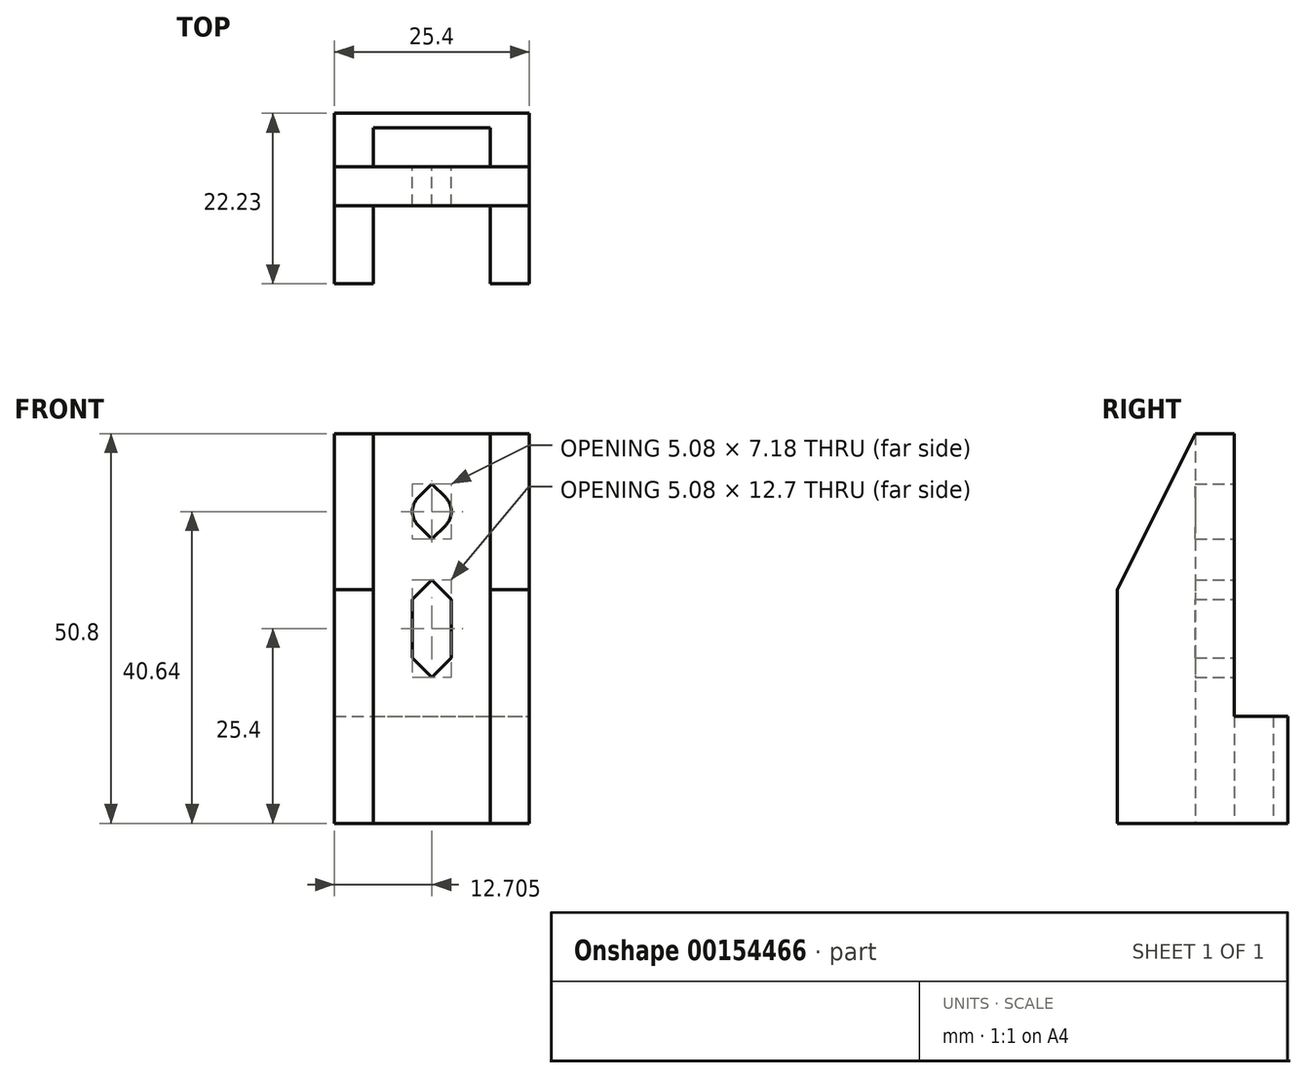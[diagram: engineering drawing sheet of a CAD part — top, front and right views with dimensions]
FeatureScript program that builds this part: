
annotation { "Feature Type Name" : "Feature", "Feature Type Description" : "" }
export const myFeature = defineFeature(function(context is Context, id is Id, definition is map)
    precondition{}
    {
        {
            var Q0;
            Q0=qCreatedBy(makeId("Top.planeOp"),FACE);
            var sketch = newSketch(context, id + "F0", { "sketchPlane" : qUnion([Q0])});
            skLineSegment(sketch, "E0.bottom", {"start": v(-5.07, -11.68) * mm, "end": v(10.17, -11.68) * mm});
            skLineSegment(sketch, "E0.top", {"start": v(-5.07, -6.6) * mm, "end": v(10.17, -6.6) * mm});
            skLineSegment(sketch, "E0.left", {"start": v(-5.07, -11.68) * mm, "end": v(-5.07, -6.6) * mm});
            skLineSegment(sketch, "E0.right", {"start": v(10.17, -11.68) * mm, "end": v(10.17, -6.6) * mm});
            skLineSegment(sketch, "E1.bottom", {"start": v(-10.15, -16.76) * mm, "end": v(15.25, -16.76) * mm});
            skLineSegment(sketch, "E1.top", {"start": v(-10.15, -4.7) * mm, "end": v(15.25, -4.7) * mm});
            skLineSegment(sketch, "E1.left", {"start": v(-10.15, -16.76) * mm, "end": v(-10.15, -4.7) * mm});
            skLineSegment(sketch, "E1.right", {"start": v(15.25, -16.76) * mm, "end": v(15.25, -4.7) * mm});
            skSolve(sketch);
        }
        {
            var Q0;
            Q0=makeQuery(id+"F0.imprint","IMPRINT",FACE,{"disambiguationData":[TD([[makeQuery(id+"F0.imprint","IMPRINT",EDGE,{"derivedFrom":sQuery(id+"F0.wireOp",EDGE,"E0.bottom")}),-1.0]])]});
            extrude(context, id + "F1", {"entities" : qUnion([Q0]), "depth" : 101.6 * mm});
        }
        {
            var Q0;
            Q0=qCreatedBy(makeId("Top.planeOp"),FACE);
            var sketch = newSketch(context, id + "F6", { "sketchPlane" : qUnion([Q0])});
            skLineSegment(sketch, "E2.bottom", {"start": v(-10.15, -16.76) * mm, "end": v(-5.07, -16.76) * mm});
            skLineSegment(sketch, "E2.top", {"start": v(-10.15, -26.92) * mm, "end": v(-5.07, -26.92) * mm});
            skLineSegment(sketch, "E2.left", {"start": v(-10.15, -16.76) * mm, "end": v(-10.15, -26.92) * mm});
            skLineSegment(sketch, "E2.right", {"start": v(-5.07, -16.76) * mm, "end": v(-5.07, -26.92) * mm});
            skLineSegment(sketch, "E3.bottom", {"start": v(15.25, -16.76) * mm, "end": v(10.17, -16.76) * mm});
            skLineSegment(sketch, "E3.top", {"start": v(15.25, -26.92) * mm, "end": v(10.17, -26.92) * mm});
            skLineSegment(sketch, "E3.left", {"start": v(15.25, -16.76) * mm, "end": v(15.25, -26.92) * mm});
            skLineSegment(sketch, "E3.right", {"start": v(10.17, -16.76) * mm, "end": v(10.17, -26.92) * mm});
            skSolve(sketch);
        }
        {
            var Q0;
            Q0=qSketchRegion(id+"F6",true);
            var Q1;
            Q1=makeQuery(id+"F1.opExtrude","CAP_FACE",FACE,{"disambiguationData":[OSD([sQuery(id+"F0.wireOp",EDGE,"E0.bottom"),sQuery(id+"F0.wireOp",EDGE,"E0.top"),sQuery(id+"F0.wireOp",EDGE,"E0.left"),sQuery(id+"F0.wireOp",EDGE,"E0.right"),sQuery(id+"F0.wireOp",EDGE,"E1.bottom"),sQuery(id+"F0.wireOp",EDGE,"E1.top"),sQuery(id+"F0.wireOp",EDGE,"E1.left"),sQuery(id+"F0.wireOp",EDGE,"E1.right")])],"isStart":false});
            extrude(context, id + "F2", {"entities" : qUnion([Q0]), "operationType" : NewBodyOperationType.ADD, "endBound" : BoundingType.UP_TO_SURFACE, "endBoundEntityFace" : qUnion([Q1]), "depth" : 25.4 * mm});
        }
        {
            var Q0;
            Q0=makeQuery(id+"F2.boolean.opBoolean","MERGE",FACE,{"derivedFrom":[makeQuery(id+"F1.opExtrude","SWEPT_FACE",FACE,{"disambiguationData":[OSD([sQuery(id+"F0.wireOp",EDGE,"E1.right")])]}),makeQuery(id+"F2.opExtrude","SWEPT_FACE",FACE,{"disambiguationData":[OSD([sQuery(id+"F6.wireOp",EDGE,"E3.left")])]})]});
            var sketch = newSketch(context, id + "F3", { "sketchPlane" : qUnion([Q0])});
            skLineSegment(sketch, "E4.bottom", {"start": v(-4.7, 101.6) * mm, "end": v(-11.68, 101.6) * mm});
            skLineSegment(sketch, "E4.top", {"start": v(-4.7, 13.97) * mm, "end": v(-11.68, 13.97) * mm});
            skLineSegment(sketch, "E4.left", {"start": v(-4.7, 101.6) * mm, "end": v(-4.7, 13.97) * mm});
            skLineSegment(sketch, "E4.right", {"start": v(-11.68, 101.6) * mm, "end": v(-11.68, 13.97) * mm});
            skSolve(sketch);
        }
        {
            var Q0;
            Q0=qSketchRegion(id+"F3",true);
            var Q1;
            Q1=makeQuery(id+"F2.boolean.opBoolean","MERGE",FACE,{"derivedFrom":[makeQuery(id+"F1.opExtrude","SWEPT_FACE",FACE,{"disambiguationData":[OSD([sQuery(id+"F0.wireOp",EDGE,"E1.left")])]}),makeQuery(id+"F2.opExtrude","SWEPT_FACE",FACE,{"disambiguationData":[OSD([sQuery(id+"F6.wireOp",EDGE,"E2.left")])]})]});
            extrude(context, id + "F7", {"entities" : qUnion([Q0]), "operationType" : NewBodyOperationType.REMOVE, "endBound" : BoundingType.UP_TO_SURFACE, "oppositeDirection" : true, "endBoundEntityFace" : qUnion([Q1]), "depth" : 25.4 * mm});
        }
        {
            var Q0;
            Q0=makeQuery(id+"F2.boolean.opBoolean","MERGE",FACE,{"derivedFrom":[makeQuery(id+"F1.opExtrude","SWEPT_FACE",FACE,{"disambiguationData":[OSD([sQuery(id+"F0.wireOp",EDGE,"E1.right")])]}),makeQuery(id+"F2.opExtrude","SWEPT_FACE",FACE,{"disambiguationData":[OSD([sQuery(id+"F6.wireOp",EDGE,"E3.left")])]})]});
            var sketch = newSketch(context, id + "F4", { "sketchPlane" : qUnion([Q0])});
            skLineSegment(sketch, "E5", {"start": v(-26.92, 101.6) * mm, "end": v(-11.68, 101.6) * mm});
            skLineSegment(sketch, "E6", {"start": v(-11.68, 101.6) * mm, "end": v(-11.68, 101.6) * mm});
            skLineSegment(sketch, "E7", {"start": v(-11.68, 50.8) * mm, "end": v(-11.68, 101.6) * mm});
            skLineSegment(sketch, "E8", {"start": v(-16.76, 50.8) * mm, "end": v(-26.92, 30.48) * mm});
            skLineSegment(sketch, "E9", {"start": v(-26.92, 30.48) * mm, "end": v(-26.92, 101.6) * mm});
            skLineSegment(sketch, "E10", {"start": v(-11.68, 50.8) * mm, "end": v(-16.76, 50.8) * mm});
            skSolve(sketch);
        }
        {
            var Q0;
            Q0=makeQuery(id+"F4.imprint","IMPRINT",FACE,{"disambiguationData":[TD([[makeQuery(id+"F4.imprint","IMPRINT",EDGE,{"derivedFrom":sQuery(id+"F4.wireOp",EDGE,"E5")}),-1.0]])]});
            var Q1;
            Q1=makeQuery(id+"F2.boolean.opBoolean","MERGE",FACE,{"derivedFrom":[makeQuery(id+"F1.opExtrude","SWEPT_FACE",FACE,{"disambiguationData":[OSD([sQuery(id+"F0.wireOp",EDGE,"E1.left")])]}),makeQuery(id+"F2.opExtrude","SWEPT_FACE",FACE,{"disambiguationData":[OSD([sQuery(id+"F6.wireOp",EDGE,"E2.left")])]})]});
            extrude(context, id + "F8", {"entities" : qUnion([Q0]), "operationType" : NewBodyOperationType.REMOVE, "endBound" : BoundingType.UP_TO_SURFACE, "oppositeDirection" : true, "endBoundEntityFace" : qUnion([Q1]), "depth" : 25.4 * mm});
        }
        {
            var Q0;
            Q0=makeQuery(id+"F7.boolean.opBoolean","MERGE",FACE,{"derivedFrom":[makeQuery(id+"F1.opExtrude","SWEPT_FACE",FACE,{"disambiguationData":[OSD([sQuery(id+"F0.wireOp",EDGE,"E0.bottom")])]}),makeQuery(id+"F7.opExtrude","SWEPT_FACE",FACE,{"disambiguationData":[OSD([sQuery(id+"F3.wireOp",EDGE,"E4.right")])]})]});
            var sketch = newSketch(context, id + "F9", { "sketchPlane" : qUnion([Q0])});
            skCircle(sketch, "E11", {"center": v(-2.55, 40.64) * mm, "radius": 2.54 * mm});
            skCircle(sketch, "E12", {"center": v(-2.55, 25.4) * mm, "radius": 2.54 * mm});
            skLineSegment(sketch, "E13", {"start": v(-2.55, 40.64) * mm, "end": v(-2.55, 25.4) * mm, "construction": true});
            skLineSegment(sketch, "E14", {"start": v(-15.25, 40.64) * mm, "end": v(-2.55, 40.64) * mm, "construction": true});
            skLineSegment(sketch, "E15", {"start": v(10.15, 40.64) * mm, "end": v(-2.55, 40.64) * mm, "construction": true});
            skSolve(sketch);
        }
        {
            var Q0;
            Q0=qSketchRegion(id+"F9",true);
            extrude(context, id + "F5", {"entities" : qUnion([Q0]), "operationType" : NewBodyOperationType.REMOVE, "endBound" : BoundingType.UP_TO_NEXT, "oppositeDirection" : true, "depth" : 25.4 * mm});
        }
        {
            var Q0;
            Q0=makeQuery(id+"F7.boolean.opBoolean","MERGE",FACE,{"derivedFrom":[makeQuery(id+"F1.opExtrude","SWEPT_FACE",FACE,{"disambiguationData":[OSD([sQuery(id+"F0.wireOp",EDGE,"E0.bottom")])]}),makeQuery(id+"F7.opExtrude","SWEPT_FACE",FACE,{"disambiguationData":[OSD([sQuery(id+"F3.wireOp",EDGE,"E4.right")])]})]});
            var sketch = newSketch(context, id + "F10", { "sketchPlane" : qUnion([Q0])});
            skLineSegment(sketch, "E16.bottom", {"start": v(-0.01, 29.21) * mm, "end": v(-5.1, 29.21) * mm, "construction": true});
            skLineSegment(sketch, "E16.top", {"start": v(-0.01, 21.6) * mm, "end": v(-5.1, 21.6) * mm, "construction": true});
            skLineSegment(sketch, "E16.left", {"start": v(-0.01, 29.21) * mm, "end": v(-0.01, 21.6) * mm});
            skLineSegment(sketch, "E16.right", {"start": v(-5.1, 29.21) * mm, "end": v(-5.1, 21.6) * mm});
            skPoint(sketch, "E16.middle", {"position": v(-2.55, 25.4) * mm});
            skLineSegment(sketch, "E17", {"start": v(-5.1, 29.21) * mm, "end": v(-2.55, 31.75) * mm});
            skLineSegment(sketch, "E18", {"start": v(-2.55, 31.75) * mm, "end": v(-2.55, 31.75) * mm});
            skLineSegment(sketch, "E19", {"start": v(-0.01, 29.21) * mm, "end": v(-2.55, 31.75) * mm});
            skLineSegment(sketch, "E20", {"start": v(-0.01, 21.6) * mm, "end": v(-2.55, 19.05) * mm});
            skLineSegment(sketch, "E21", {"start": v(-2.55, 19.05) * mm, "end": v(-2.55, 19.05) * mm});
            skLineSegment(sketch, "E22", {"start": v(-2.55, 19.05) * mm, "end": v(-5.1, 21.59) * mm});
            skLineSegment(sketch, "E23", {"start": v(-4.35, 42.44) * mm, "end": v(-2.55, 44.23) * mm});
            skLineSegment(sketch, "E24", {"start": v(-2.55, 44.23) * mm, "end": v(-0.76, 42.44) * mm});
            skLineSegment(sketch, "E25", {"start": v(-4.35, 38.84) * mm, "end": v(-2.55, 37.05) * mm});
            skLineSegment(sketch, "E26", {"start": v(-2.55, 37.05) * mm, "end": v(-0.76, 38.84) * mm});
            skLineSegment(sketch, "E27", {"start": v(-4.35, 42.44) * mm, "end": v(-0.76, 42.44) * mm});
            skLineSegment(sketch, "E28", {"start": v(-0.76, 38.84) * mm, "end": v(-4.35, 38.84) * mm});
            skSolve(sketch);
        }
        {
            var Q0;
            Q0=qSketchRegion(id+"F10",true);
            var Q1;
            Q1=makeQuery(id+"F1.opExtrude","SWEPT_FACE",FACE,{"disambiguationData":[OSD([sQuery(id+"F0.wireOp",EDGE,"E1.bottom")])]});
            extrude(context, id + "F11", {"entities" : qUnion([Q0]), "operationType" : NewBodyOperationType.REMOVE, "endBound" : BoundingType.UP_TO_SURFACE, "oppositeDirection" : true, "endBoundEntityFace" : qUnion([Q1]), "depth" : 25.4 * mm});
        }
    });
